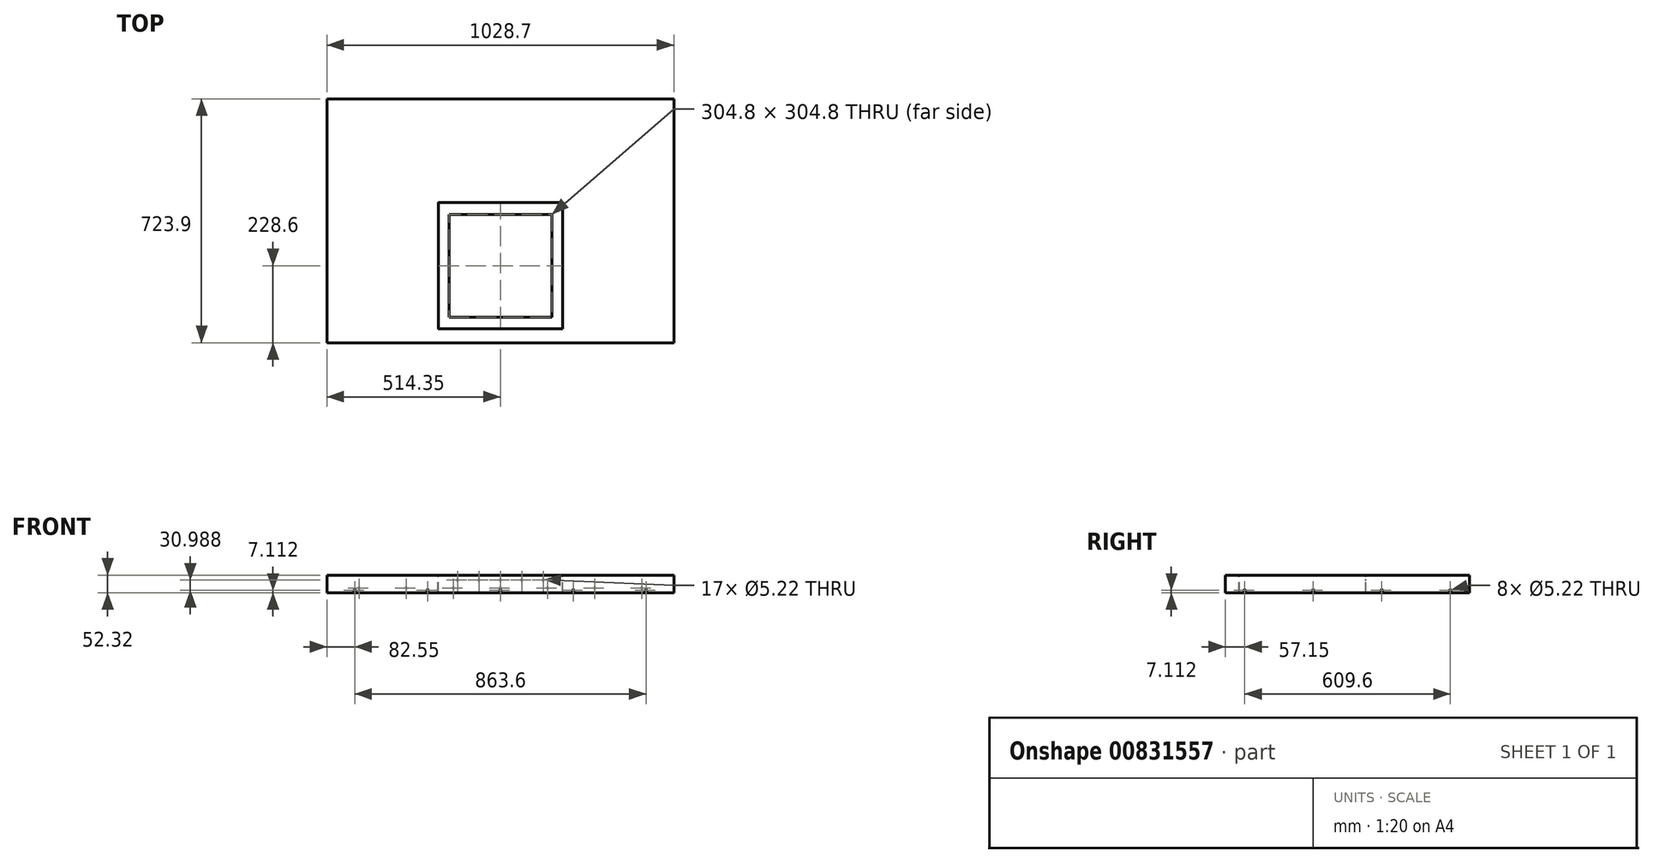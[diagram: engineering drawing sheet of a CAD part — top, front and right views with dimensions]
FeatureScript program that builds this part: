
annotation { "Feature Type Name" : "Feature", "Feature Type Description" : "" }
export const myFeature = defineFeature(function(context is Context, id is Id, definition is map)
    precondition{}
    {
        {
            var Q0;
            Q0=qCreatedBy(makeId("Top.planeOp"),FACE);
            var sketch = newSketch(context, id + "F0", { "sketchPlane" : qUnion([Q0])});
            skLineSegment(sketch, "E0.top", {"start": v(-514.35, -361.95) * mm, "end": v(514.35, -361.95) * mm});
            skLineSegment(sketch, "E0.left", {"start": v(-514.35, 361.95) * mm, "end": v(-514.35, -361.95) * mm});
            skLineSegment(sketch, "E0.right", {"start": v(514.35, 361.95) * mm, "end": v(514.35, -361.95) * mm});
            skLineSegment(sketch, "E1", {"start": v(-514.35, 361.95) * mm, "end": v(514.35, 361.95) * mm});
            skLineSegment(sketch, "E2", {"start": v(0, -361.95) * mm, "end": v(0, 0) * mm});
            skLineSegment(sketch, "E3", {"start": v(0, 0) * mm, "end": v(0, 361.95) * mm});
            skSolve(sketch);
        }
        {
            var Q0;
            Q0=qSketchRegion(id+"F0",true);
            extrude(context, id + "F1", {"entities" : qUnion([Q0]), "depth" : 52.32 * mm, "offsetDistance" : 25.4 * mm});
        }
        {
            var Q0;
            Q0=makeQuery(id+"F1.opExtrude","CAP_FACE",FACE,{"disambiguationData":[OSD([sQuery(id+"F0.wireOp",EDGE,"E0.top"),sQuery(id+"F0.wireOp",EDGE,"E0.left"),sQuery(id+"F0.wireOp",EDGE,"E0.right"),sQuery(id+"F0.wireOp",EDGE,"9ab933a8-7917-4582-8853-033de83bfb6f.filletArc"),sQuery(id+"F0.wireOp",EDGE,"2fbcc5d7-b81c-47a4-a430-0d7138a8ee22.filletArc"),sQuery(id+"F0.wireOp",EDGE,"6fea4ef0-73c7-4de9-b055-764364034492.filletArc"),sQuery(id+"F0.wireOp",EDGE,"411982ff-6128-4dcf-929b-ad70442d3dd5.filletArc"),sQuery(id+"F0.wireOp",EDGE,"E1")])],"isStart":true});
            shell(context, id + "F2", {"entities" : qUnion([Q0]), "thickness" : 1.27 * mm});
        }
        {
            var Q0;
            Q0=makeQuery(id+"F1.opExtrude","SWEPT_FACE",FACE,{"disambiguationData":[OSD([sQuery(id+"F0.wireOp",EDGE,"E0.top")])]});
            var sketch = newSketch(context, id + "F3", { "sketchPlane" : qUnion([Q0])});
            skPoint(sketch, "E4", {"position": v(0, 7.11) * mm});
            skPoint(sketch, "E5", {"position": v(431.8, 7.11) * mm});
            skPoint(sketch, "E6", {"position": v(-431.8, 7.11) * mm});
            skPoint(sketch, "E7", {"position": v(-215.9, 7.11) * mm});
            skPoint(sketch, "E8", {"position": v(215.9, 7.11) * mm});
            skLineSegment(sketch, "E9", {"start": v(-431.8, 7.11) * mm, "end": v(-215.9, 7.11) * mm});
            skLineSegment(sketch, "E10", {"start": v(0, 7.11) * mm, "end": v(-215.9, 7.11) * mm});
            skLineSegment(sketch, "E11", {"start": v(0, 7.11) * mm, "end": v(215.9, 7.11) * mm});
            skLineSegment(sketch, "E12", {"start": v(215.9, 7.11) * mm, "end": v(431.8, 7.11) * mm});
            skSolve(sketch);
        }
        {
            var Q0;
            Q0=sQuery(id+"F3.wireOp",VERTEX,"E6");
            var Q1;
            Q1=sQuery(id+"F3.wireOp",VERTEX,"E7");
            var Q2;
            Q2=sQuery(id+"F3.wireOp",VERTEX,"E4");
            var Q3;
            Q3=sQuery(id+"F3.wireOp",VERTEX,"E8");
            var Q4;
            Q4=sQuery(id+"F3.wireOp",VERTEX,"E5");
            var Q5;
            Q5=makeQuery(id+"F1.opExtrude","SWEPT_BODY",BODY,{"disambiguationData":[OSD([sQuery(id+"F0.wireOp",EDGE,"E0.top"),sQuery(id+"F0.wireOp",EDGE,"E0.left"),sQuery(id+"F0.wireOp",EDGE,"E0.right"),sQuery(id+"F0.wireOp",EDGE,"9ab933a8-7917-4582-8853-033de83bfb6f.filletArc"),sQuery(id+"F0.wireOp",EDGE,"2fbcc5d7-b81c-47a4-a430-0d7138a8ee22.filletArc"),sQuery(id+"F0.wireOp",EDGE,"6fea4ef0-73c7-4de9-b055-764364034492.filletArc"),sQuery(id+"F0.wireOp",EDGE,"411982ff-6128-4dcf-929b-ad70442d3dd5.filletArc"),sQuery(id+"F0.wireOp",EDGE,"E1")])]});
            hole(context, id + "F4", {"style" : HoleStyle.SIMPLE, "endStyle" : HoleEndStyle.BLIND, "standardTappedOrClearance" : lookupTablePath({ "standard" : "ANSI", "size" : "#5 (0.2)", "type" : "Drilled" }), "standardBlindInLast" : lookupTablePath({ "standard" : "ANSI", "size" : "#5 (0.2)", "type" : "Drilled" }), "holeDiameter" : 5.22 * mm, "majorDiameter" : 6.35 * mm, "holeDepth" : 0.76 * mm, "isTappedThrough" : true, "tappedDepth" : 12.7 * mm, "tapClearance" : 3, "locations" : qUnion([Q0, Q1, Q2, Q3, Q4]), "scope" : qUnion([Q5])});
        }
        {
            var Q0;
            Q0=makeQuery(id+"F1.opExtrude","SWEPT_FACE",FACE,{"disambiguationData":[OSD([sQuery(id+"F0.wireOp",EDGE,"E0.right")])]});
            var sketch = newSketch(context, id + "F5", { "sketchPlane" : qUnion([Q0])});
            skPoint(sketch, "E13", {"position": v(-304.8, 7.11) * mm});
            skPoint(sketch, "E14", {"position": v(-101.6, 7.11) * mm});
            skPoint(sketch, "E15", {"position": v(101.6, 7.11) * mm});
            skPoint(sketch, "E16", {"position": v(304.8, 7.11) * mm});
            skLineSegment(sketch, "E17", {"start": v(-304.8, 7.11) * mm, "end": v(-101.6, 7.11) * mm});
            skLineSegment(sketch, "E18", {"start": v(-101.6, 7.11) * mm, "end": v(101.6, 7.11) * mm});
            skLineSegment(sketch, "E19", {"start": v(101.6, 7.11) * mm, "end": v(304.8, 7.11) * mm});
            skLineSegment(sketch, "E20", {"start": v(0, 7.11) * mm, "end": v(0, 0) * mm});
            skSolve(sketch);
        }
        {
            var Q0;
            Q0=sQuery(id+"F5.wireOp",VERTEX,"E13");
            var Q1;
            Q1=sQuery(id+"F5.wireOp",VERTEX,"E14");
            var Q2;
            Q2=sQuery(id+"F5.wireOp",VERTEX,"E15");
            var Q3;
            Q3=sQuery(id+"F5.wireOp",VERTEX,"E16");
            var Q4;
            Q4=makeQuery(id+"F1.opExtrude","SWEPT_BODY",BODY,{"disambiguationData":[OSD([sQuery(id+"F0.wireOp",EDGE,"E0.top"),sQuery(id+"F0.wireOp",EDGE,"E0.left"),sQuery(id+"F0.wireOp",EDGE,"E0.right"),sQuery(id+"F0.wireOp",EDGE,"E1")])]});
            hole(context, id + "F6", {"style" : HoleStyle.SIMPLE, "endStyle" : HoleEndStyle.THROUGH, "standardTappedOrClearance" : lookupTablePath({ "standard" : "ANSI", "size" : "#5 (0.2)", "type" : "Drilled" }), "standardBlindInLast" : lookupTablePath({ "standard" : "ANSI", "size" : "#5 (0.2)", "type" : "Drilled" }), "holeDiameter" : 5.22 * mm, "majorDiameter" : 6.35 * mm, "isTappedThrough" : true, "tappedDepth" : 12.7 * mm, "tapClearance" : 3, "locations" : qUnion([Q0, Q1, Q2, Q3]), "scope" : qUnion([Q4])});
        }
        {
            var Q0;
            Q0=makeQuery(id+"F1.opExtrude","CAP_FACE",FACE,{"disambiguationData":[OSD([sQuery(id+"F0.wireOp",EDGE,"E0.top"),sQuery(id+"F0.wireOp",EDGE,"E0.left"),sQuery(id+"F0.wireOp",EDGE,"E0.right"),sQuery(id+"F0.wireOp",EDGE,"9ab933a8-7917-4582-8853-033de83bfb6f.filletArc"),sQuery(id+"F0.wireOp",EDGE,"2fbcc5d7-b81c-47a4-a430-0d7138a8ee22.filletArc"),sQuery(id+"F0.wireOp",EDGE,"6fea4ef0-73c7-4de9-b055-764364034492.filletArc"),sQuery(id+"F0.wireOp",EDGE,"411982ff-6128-4dcf-929b-ad70442d3dd5.filletArc"),sQuery(id+"F0.wireOp",EDGE,"E1")])],"isStart":false});
            var sketch = newSketch(context, id + "F7", { "sketchPlane" : qUnion([Q0])});
            skLineSegment(sketch, "E21.bottom", {"start": v(-184.15, 53.97) * mm, "end": v(184.15, 53.97) * mm});
            skLineSegment(sketch, "E21.top", {"start": v(-184.15, -320.68) * mm, "end": v(184.15, -320.68) * mm});
            skLineSegment(sketch, "E21.left", {"start": v(-184.15, 53.97) * mm, "end": v(-184.15, -320.68) * mm});
            skLineSegment(sketch, "E21.right", {"start": v(184.15, 53.97) * mm, "end": v(184.15, -320.68) * mm});
            skLineSegment(sketch, "E22", {"start": v(-184.15, -133.35) * mm, "end": v(184.15, -133.35) * mm, "construction": true});
            skLineSegment(sketch, "E23", {"start": v(0, -320.68) * mm, "end": v(0, 53.97) * mm, "construction": true});
            skLineSegment(sketch, "E24", {"start": v(-514.35, 0) * mm, "end": v(0, 0) * mm, "construction": true});
            skLineSegment(sketch, "E25", {"start": v(0, 0) * mm, "end": v(514.35, 0) * mm, "construction": true});
            skSolve(sketch);
        }
        {
            var Q0;
            Q0=qSketchRegion(id+"F7",true);
            extrude(context, id + "F8", {"entities" : qUnion([Q0]), "operationType" : NewBodyOperationType.REMOVE, "endBound" : BoundingType.THROUGH_ALL, "oppositeDirection" : true, "depth" : 25.4 * mm, "offsetDistance" : 25.4 * mm});
        }
        {
            var Q0;
            Q0=makeQuery(id+"F1.opExtrude","CAP_FACE",FACE,{"disambiguationData":[OSD([sQuery(id+"F0.wireOp",EDGE,"E0.top"),sQuery(id+"F0.wireOp",EDGE,"E0.left"),sQuery(id+"F0.wireOp",EDGE,"E0.right"),sQuery(id+"F0.wireOp",EDGE,"E1")])],"isStart":false});
            var sketch = newSketch(context, id + "F9", { "sketchPlane" : qUnion([Q0])});
            skLineSegment(sketch, "E26.bottom", {"start": v(184.15, -320.68) * mm, "end": v(-184.15, -320.68) * mm});
            skLineSegment(sketch, "E26.top", {"start": v(184.15, 53.98) * mm, "end": v(-184.15, 53.97) * mm});
            skLineSegment(sketch, "E26.left", {"start": v(184.15, -320.68) * mm, "end": v(184.15, 53.98) * mm});
            skLineSegment(sketch, "E26.right", {"start": v(-184.15, -320.68) * mm, "end": v(-184.15, 53.97) * mm});
            skLineSegment(sketch, "E27.bottom", {"start": v(-184.91, -321.44) * mm, "end": v(184.91, -321.44) * mm});
            skLineSegment(sketch, "E27.top", {"start": v(-184.91, 54.74) * mm, "end": v(184.91, 54.74) * mm});
            skLineSegment(sketch, "E27.left", {"start": v(-184.91, -321.44) * mm, "end": v(-184.91, 54.74) * mm});
            skLineSegment(sketch, "E27.right", {"start": v(184.91, -321.44) * mm, "end": v(184.91, 54.74) * mm});
            skSolve(sketch);
        }
        {
            var Q0;
            Q0=qSketchRegion(id+"F9",true);
            extrude(context, id + "F10", {"entities" : qUnion([Q0]), "operationType" : NewBodyOperationType.ADD, "oppositeDirection" : true, "depth" : 51.56 * mm, "offsetDistance" : 25.4 * mm});
        }
        {
            var Q0;
            Q0=makeQuery(id+"F10.opExtrude","CAP_FACE",FACE,{"disambiguationData":[OSD([sQuery(id+"F9.wireOp",EDGE,"E26.bottom"),sQuery(id+"F9.wireOp",EDGE,"E26.top"),sQuery(id+"F9.wireOp",EDGE,"E26.left"),sQuery(id+"F9.wireOp",EDGE,"E26.right"),sQuery(id+"F9.wireOp",EDGE,"E27.bottom"),sQuery(id+"F9.wireOp",EDGE,"E27.top"),sQuery(id+"F9.wireOp",EDGE,"E27.left"),sQuery(id+"F9.wireOp",EDGE,"E27.right")])],"isStart":false});
            var sketch = newSketch(context, id + "F11", { "sketchPlane" : qUnion([Q0])});
            skLineSegment(sketch, "E28.bottom", {"start": v(-152.4, 285.75) * mm, "end": v(152.4, 285.75) * mm});
            skLineSegment(sketch, "E28.top", {"start": v(-152.4, -19.05) * mm, "end": v(152.4, -19.05) * mm});
            skLineSegment(sketch, "E28.left", {"start": v(-152.4, 285.75) * mm, "end": v(-152.4, -19.05) * mm});
            skLineSegment(sketch, "E28.right", {"start": v(152.4, 285.75) * mm, "end": v(152.4, -19.05) * mm});
            skLineSegment(sketch, "E29.bottom", {"start": v(-184.91, 321.44) * mm, "end": v(184.91, 321.44) * mm});
            skLineSegment(sketch, "E29.top", {"start": v(-184.91, -54.74) * mm, "end": v(184.91, -54.74) * mm});
            skLineSegment(sketch, "E29.left", {"start": v(-184.91, 321.44) * mm, "end": v(-184.91, -54.74) * mm});
            skLineSegment(sketch, "E29.right", {"start": v(184.91, 321.44) * mm, "end": v(184.91, -54.74) * mm});
            skLineSegment(sketch, "E30", {"start": v(0, 320.68) * mm, "end": v(0, 285.75) * mm, "construction": true});
            skLineSegment(sketch, "E31", {"start": v(0, -53.97) * mm, "end": v(0, -19.05) * mm, "construction": true});
            skSolve(sketch);
        }
        {
            var Q0;
            Q0=makeQuery(id+"F11.imprint","IMPRINT",FACE,{"disambiguationData":[TD([[makeQuery(id+"F11.imprint","IMPRINT",EDGE,{"derivedFrom":sQuery(id+"F11.wireOp",EDGE,"E28.bottom")}),1.0]])]});
            extrude(context, id + "F12", {"entities" : qUnion([Q0]), "operationType" : NewBodyOperationType.ADD, "oppositeDirection" : true, "depth" : 0.76 * mm, "offsetDistance" : 25.4 * mm});
        }
        {
            var Q0;
            Q0=makeQuery(id+"F1.opExtrude","SWEPT_FACE",FACE,{"disambiguationData":[OSD([sQuery(id+"F0.wireOp",EDGE,"E1")])]});
            var sketch = newSketch(context, id + "F13", { "sketchPlane" : qUnion([Q0])});
            skPoint(sketch, "E32", {"position": v(-419.1, 14.29) * mm});
            skPoint(sketch, "E33", {"position": v(-279.4, 14.29) * mm});
            skPoint(sketch, "E34", {"position": v(-139.7, 14.29) * mm});
            skPoint(sketch, "E35", {"position": v(0, 14.29) * mm});
            skPoint(sketch, "E36", {"position": v(139.7, 14.29) * mm});
            skPoint(sketch, "E37", {"position": v(279.4, 14.29) * mm});
            skPoint(sketch, "E38", {"position": v(419.1, 14.29) * mm});
            skLineSegment(sketch, "E39", {"start": v(-514.35, 14.29) * mm, "end": v(-419.1, 14.29) * mm});
            skLineSegment(sketch, "E40", {"start": v(-279.4, 14.29) * mm, "end": v(-419.1, 14.29) * mm});
            skLineSegment(sketch, "E41", {"start": v(-279.4, 14.29) * mm, "end": v(-139.7, 14.29) * mm});
            skLineSegment(sketch, "E42", {"start": v(-139.7, 14.29) * mm, "end": v(0, 14.29) * mm});
            skLineSegment(sketch, "E43", {"start": v(0, 14.29) * mm, "end": v(139.7, 14.29) * mm});
            skLineSegment(sketch, "E44", {"start": v(139.7, 14.29) * mm, "end": v(279.4, 14.29) * mm});
            skLineSegment(sketch, "E45", {"start": v(279.4, 14.29) * mm, "end": v(419.1, 14.29) * mm});
            skLineSegment(sketch, "E46", {"start": v(419.1, 14.29) * mm, "end": v(514.35, 14.29) * mm});
            skSolve(sketch);
        }
        {
            var Q0;
            Q0=sQuery(id+"F13.wireOp",VERTEX,"E40.end");
            var Q1;
            Q1=sQuery(id+"F13.wireOp",VERTEX,"E33");
            var Q2;
            Q2=sQuery(id+"F13.wireOp",VERTEX,"E34");
            var Q3;
            Q3=sQuery(id+"F13.wireOp",VERTEX,"E35");
            var Q4;
            Q4=sQuery(id+"F13.wireOp",VERTEX,"E43.end");
            var Q5;
            Q5=sQuery(id+"F13.wireOp",VERTEX,"E37");
            var Q6;
            Q6=sQuery(id+"F13.wireOp",VERTEX,"E38");
            var Q7;
            Q7=makeQuery(id+"F1.opExtrude","SWEPT_BODY",BODY,{"disambiguationData":[OSD([sQuery(id+"F0.wireOp",EDGE,"E0.top"),sQuery(id+"F0.wireOp",EDGE,"E0.left"),sQuery(id+"F0.wireOp",EDGE,"E0.right"),sQuery(id+"F0.wireOp",EDGE,"E1")])]});
            hole(context, id + "F14", {"style" : HoleStyle.SIMPLE, "endStyle" : HoleEndStyle.BLIND, "standardTappedOrClearance" : lookupTablePath({ "standard" : "ANSI", "size" : "#5 (0.2)", "type" : "Drilled" }), "standardBlindInLast" : lookupTablePath({ "standard" : "ANSI", "size" : "#5 (0.2)", "type" : "Drilled" }), "holeDiameter" : 5.22 * mm, "majorDiameter" : 6.35 * mm, "holeDepth" : 0.76 * mm, "isTappedThrough" : true, "tappedDepth" : 12.7 * mm, "tapClearance" : 3, "locations" : qUnion([Q0, Q1, Q2, Q3, Q4, Q5, Q6]), "scope" : qUnion([Q7])});
        }
        {
            var Q0;
            Q0=makeQuery(id+"F10.boolean.opBoolean","MERGE",FACE,{"derivedFrom":[makeQuery(id+"F8.boolean.opBoolean","COPY",FACE,{"derivedFrom":makeQuery(id+"F8.opExtrude","SWEPT_FACE",FACE,{"disambiguationData":[OSD([sQuery(id+"F7.wireOp",EDGE,"E21.bottom")])]})}),makeQuery(id+"F10.opExtrude","SWEPT_FACE",FACE,{"disambiguationData":[OSD([sQuery(id+"F9.wireOp",EDGE,"E26.top")])]})]});
            var sketch = newSketch(context, id + "F15", { "sketchPlane" : qUnion([Q0])});
            skPoint(sketch, "E47", {"position": v(-127, 38.1) * mm});
            skPoint(sketch, "E48", {"position": v(-63.5, 38.1) * mm});
            skPoint(sketch, "E49", {"position": v(0, 38.1) * mm});
            skPoint(sketch, "E50", {"position": v(63.5, 38.1) * mm});
            skPoint(sketch, "E51", {"position": v(127, 38.1) * mm});
            skLineSegment(sketch, "E52", {"start": v(-127, 38.1) * mm, "end": v(-63.5, 38.1) * mm});
            skLineSegment(sketch, "E53", {"start": v(-63.5, 38.1) * mm, "end": v(0, 38.1) * mm});
            skLineSegment(sketch, "E54", {"start": v(0, 38.1) * mm, "end": v(63.5, 38.1) * mm});
            skLineSegment(sketch, "E55", {"start": v(63.5, 38.1) * mm, "end": v(127, 38.1) * mm});
            skLineSegment(sketch, "E56", {"start": v(0, 38.1) * mm, "end": v(0, 52.32) * mm});
            skSolve(sketch);
        }
        {
            var Q0;
            Q0=sQuery(id+"F15.wireOp",VERTEX,"E47");
            var Q1;
            Q1=sQuery(id+"F15.wireOp",VERTEX,"E48");
            var Q2;
            Q2=sQuery(id+"F15.wireOp",VERTEX,"E49");
            var Q3;
            Q3=sQuery(id+"F15.wireOp",VERTEX,"E50");
            var Q4;
            Q4=sQuery(id+"F15.wireOp",VERTEX,"E51");
            var Q5;
            Q5=makeQuery(id+"F1.opExtrude","SWEPT_BODY",BODY,{"disambiguationData":[OSD([sQuery(id+"F0.wireOp",EDGE,"E0.top"),sQuery(id+"F0.wireOp",EDGE,"E0.left"),sQuery(id+"F0.wireOp",EDGE,"E0.right"),sQuery(id+"F0.wireOp",EDGE,"E1")])]});
            hole(context, id + "F16", {"style" : HoleStyle.SIMPLE, "endStyle" : HoleEndStyle.BLIND, "standardTappedOrClearance" : lookupTablePath({ "standard" : "ANSI", "size" : "#5 (0.2)", "type" : "Drilled" }), "standardBlindInLast" : lookupTablePath({ "standard" : "ANSI", "size" : "#5 (0.2)", "type" : "Drilled" }), "holeDiameter" : 5.22 * mm, "majorDiameter" : 6.35 * mm, "holeDepth" : 0.76 * mm, "isTappedThrough" : true, "tappedDepth" : 12.7 * mm, "tapClearance" : 3, "locations" : qUnion([Q0, Q1, Q2, Q3, Q4]), "scope" : qUnion([Q5])});
        }
    });
